# Revit family: RN 81084 Optipress-Segment de tuyau en acier inoxydable
name_source: partatom
category: Rohrformteile
units: mm (PartAtom-declared; Revit-internal decimal feet)

## family parameters
Arbeitsebenenbasiert = Nein
Beim Laden mit Abzugskörper schneiden = Nein
Bemaßung runder Anschluss = Durchmesser verwenden
Gemeinsam genutzt = Nein
Immer vertikal = Ja
Teiletyp = Nicht definiert

## types (11) — shared parameters
1.010.00.2 Number of the part of the guideline = 29
1.010.00.3 Issue date (month) of the guideline = 201308
1.010.00.4 Manufacturer name = R. Nussbaum AG
1.010.00.5 Revision date of the file = 20201220
1.100.00.4 Product designation = Optipress-Segment de tuyau en acier inoxydable
1.110.00.2 Index = 4
1.110.00.4 Product designation = Optipress
1.960/3L.00.8 Link (URL) = https://www.nussbaum.ch
29.700.00.4 Product name = Optipress-Segment de tuyau en acier inoxydable
29.700.00.5 Product identification = 2
29.700.00.6 Cross-sectional shape = 1
29.700.00.7 Nominal size system = DN
29.700.00.8 Nominal pressure system = PN
29.710.02.4 Nominal pressure = 16
29.710.02.5 max. allowed overpressure [hPa] = 1600
29.710.02.7 max. allowed continuous operating pressure [hPa] = 1600
29.710.02.9 max. allowed continuous operating temperature [°C] = 95
Connector Visibility = Nein
EnclosingSpace Visibility = Nein
Hersteller = R. Nussbaum AG
Typenkommentare = Optipress-Segment de tuyau en acier inoxydable
URL = https://www.nussbaum.ch

## per-type parameters (varying)
- DN=80: 1.800.00.3 BS number=01900400000000000000000000000000000000000000000055000000000000000009; 1.800.00.4 Comment field=81084.30, OP-Pezzo di tubo in acciaio inossidabile, DN=80, L=115; 1.810.00.3 Manufacturer’s reference number=81084.30; 1.810.00.4 DATANORM number=81084.30; 1.810.00.5 StLB number=261.152; 1.810.00.6 GTIN number=7612945692375; 29.710.02.10 Fitting weight [kg]=0.494; 29.710.02.3 Designation=OP-Pezzo di tubo in acciaio inossidabile, DN=80, L=115; CONNECTOR0_DIAMETER_dX_0r=80 mm; CONNECTOR0_dX_01=50 mm; CONNECTOR0_ref_dX=50 mm; CONNECTOR1_DIAMETER_dX_0r=80 mm; CONNECTOR1_dX_00=65 mm  [stored 0.213255 ft]; CONNECTOR1_dX_01=115 mm; CONNECTOR1_ref_dX=65 mm  [stored 0.213255 ft]; Modell=81084.30; R. Nussbaum AG 81084.22 it Visibility=Nein; R. Nussbaum AG 81084.23 it Visibility=Nein; R. Nussbaum AG 81084.24 it Visibility=Nein; R. Nussbaum AG 81084.25 it Visibility=Nein; R. Nussbaum AG 81084.26 it Visibility=Nein; R. Nussbaum AG 81084.27 it Visibility=Nein; R. Nussbaum AG 81084.28 it Visibility=Nein; R. Nussbaum AG 81084.29 it Visibility=Nein; R. Nussbaum AG 81084.30 it Visibility=Ja; R. Nussbaum AG 81084.31 it Visibility=Nein; R. Nussbaum AG 81084.32 it Visibility=Nein
- DN=60: 1.800.00.3 BS number=01900400000000000000000000000000000000000000000055000000000000000011; 1.800.00.4 Comment field=81084.32, OP-Pezzo di tubo in acciaio inossidabile, DN=60, L=101; 1.810.00.3 Manufacturer’s reference number=81084.32; 1.810.00.4 DATANORM number=81084.32; 1.810.00.5 StLB number=261.154; 1.810.00.6 GTIN number=7612945692351; 29.710.02.10 Fitting weight [kg]=0.307; 29.710.02.3 Designation=OP-Pezzo di tubo in acciaio inossidabile, DN=60, L=101; CONNECTOR0_DIAMETER_dX_0r=60 mm; CONNECTOR0_dX_01=43 mm  [stored 0.141076 ft]; CONNECTOR0_ref_dX=43 mm  [stored 0.141076 ft]; CONNECTOR1_DIAMETER_dX_0r=60 mm; CONNECTOR1_dX_00=58 mm; CONNECTOR1_dX_01=101 mm; CONNECTOR1_ref_dX=58 mm; Modell=81084.32; R. Nussbaum AG 81084.22 it Visibility=Nein; R. Nussbaum AG 81084.23 it Visibility=Nein; R. Nussbaum AG 81084.24 it Visibility=Nein; R. Nussbaum AG 81084.25 it Visibility=Nein; R. Nussbaum AG 81084.26 it Visibility=Nein; R. Nussbaum AG 81084.27 it Visibility=Nein; R. Nussbaum AG 81084.28 it Visibility=Nein; R. Nussbaum AG 81084.29 it Visibility=Nein; R. Nussbaum AG 81084.30 it Visibility=Nein; R. Nussbaum AG 81084.31 it Visibility=Nein; R. Nussbaum AG 81084.32 it Visibility=Ja
- DN=100: 1.800.00.3 BS number=01900400000000000000000000000000000000000000000055000000000000000010; 1.800.00.4 Comment field=81084.31, OP-Pezzo di tubo in acciaio inossidabile, DN=100, L=135; 1.810.00.3 Manufacturer’s reference number=81084.31; 1.810.00.4 DATANORM number=81084.31; 1.810.00.5 StLB number=261.153; 1.810.00.6 GTIN number=7612945692382; 29.710.02.10 Fitting weight [kg]=0.705; 29.710.02.3 Designation=OP-Pezzo di tubo in acciaio inossidabile, DN=100, L=135; CONNECTOR0_DIAMETER_dX_0r=100 mm  [stored 0.328084 ft]; CONNECTOR0_dX_01=60 mm; CONNECTOR0_ref_dX=60 mm; CONNECTOR1_DIAMETER_dX_0r=100 mm  [stored 0.328084 ft]; CONNECTOR1_dX_00=75 mm; CONNECTOR1_dX_01=135 mm; CONNECTOR1_ref_dX=75 mm; Modell=81084.31; R. Nussbaum AG 81084.22 it Visibility=Nein; R. Nussbaum AG 81084.23 it Visibility=Nein; R. Nussbaum AG 81084.24 it Visibility=Nein; R. Nussbaum AG 81084.25 it Visibility=Nein; R. Nussbaum AG 81084.26 it Visibility=Nein; R. Nussbaum AG 81084.27 it Visibility=Nein; R. Nussbaum AG 81084.28 it Visibility=Nein; R. Nussbaum AG 81084.29 it Visibility=Nein; R. Nussbaum AG 81084.30 it Visibility=Nein; R. Nussbaum AG 81084.31 it Visibility=Ja; R. Nussbaum AG 81084.32 it Visibility=Nein
- DN=65: 1.800.00.3 BS number=01900400000000000000000000000000000000000000000055000000000000000008; 1.800.00.4 Comment field=81084.29, OP-Pezzo di tubo in acciaio inossidabile, DN=65, L=115; 1.810.00.3 Manufacturer’s reference number=81084.29; 1.810.00.4 DATANORM number=81084.29; 1.810.00.5 StLB number=261.151; 1.810.00.6 GTIN number=7612945692368; 29.710.02.10 Fitting weight [kg]=0.426; 29.710.02.3 Designation=OP-Pezzo di tubo in acciaio inossidabile, DN=65, L=115; CONNECTOR0_DIAMETER_dX_0r=65 mm  [stored 0.213255 ft]; CONNECTOR0_dX_01=50 mm; CONNECTOR0_ref_dX=50 mm; CONNECTOR1_DIAMETER_dX_0r=65 mm  [stored 0.213255 ft]; CONNECTOR1_dX_00=65 mm  [stored 0.213255 ft]; CONNECTOR1_dX_01=115 mm; CONNECTOR1_ref_dX=65 mm  [stored 0.213255 ft]; Modell=81084.29; R. Nussbaum AG 81084.22 it Visibility=Nein; R. Nussbaum AG 81084.23 it Visibility=Nein; R. Nussbaum AG 81084.24 it Visibility=Nein; R. Nussbaum AG 81084.25 it Visibility=Nein; R. Nussbaum AG 81084.26 it Visibility=Nein; R. Nussbaum AG 81084.27 it Visibility=Nein; R. Nussbaum AG 81084.28 it Visibility=Nein; R. Nussbaum AG 81084.29 it Visibility=Ja; R. Nussbaum AG 81084.30 it Visibility=Nein; R. Nussbaum AG 81084.31 it Visibility=Nein; R. Nussbaum AG 81084.32 it Visibility=Nein
- DN=50: 1.800.00.3 BS number=01900400000000000000000000000000000000000000000055000000000000000007; 1.800.00.4 Comment field=81084.28, OP-Pezzo di tubo in acciaio inossidabile, DN=50, L=105; 1.810.00.3 Manufacturer’s reference number=81084.28; 1.810.00.4 DATANORM number=81084.28; 1.810.00.5 StLB number=261.148; 1.810.00.6 GTIN number=7612945692344; 29.710.02.10 Fitting weight [kg]=0.204; 29.710.02.3 Designation=OP-Pezzo di tubo in acciaio inossidabile, DN=50, L=105; CONNECTOR0_DIAMETER_dX_0r=50 mm; CONNECTOR0_dX_01=40 mm; CONNECTOR0_ref_dX=40 mm; CONNECTOR1_DIAMETER_dX_0r=50 mm; CONNECTOR1_dX_00=65 mm  [stored 0.213255 ft]; CONNECTOR1_dX_01=105 mm; CONNECTOR1_ref_dX=65 mm  [stored 0.213255 ft]; Modell=81084.28; R. Nussbaum AG 81084.22 it Visibility=Nein; R. Nussbaum AG 81084.23 it Visibility=Nein; R. Nussbaum AG 81084.24 it Visibility=Nein; R. Nussbaum AG 81084.25 it Visibility=Nein; R. Nussbaum AG 81084.26 it Visibility=Nein; R. Nussbaum AG 81084.27 it Visibility=Nein; R. Nussbaum AG 81084.28 it Visibility=Ja; R. Nussbaum AG 81084.29 it Visibility=Nein; R. Nussbaum AG 81084.30 it Visibility=Nein; R. Nussbaum AG 81084.31 it Visibility=Nein; R. Nussbaum AG 81084.32 it Visibility=Nein
- DN=40: 1.800.00.3 BS number=01900400000000000000000000000000000000000000000055000000000000000006; 1.800.00.4 Comment field=81084.27, OP-Pezzo di tubo in acciaio inossidabile, DN=40, L=87; 1.810.00.3 Manufacturer’s reference number=81084.27; 1.810.00.4 DATANORM number=81084.27; 1.810.00.5 StLB number=261.147; 1.810.00.6 GTIN number=7612945692337; 29.710.02.10 Fitting weight [kg]=0.124; 29.710.02.3 Designation=OP-Pezzo di tubo in acciaio inossidabile, DN=40, L=87; CONNECTOR0_DIAMETER_dX_0r=40 mm; CONNECTOR0_dX_01=36 mm  [stored 0.11811 ft]; CONNECTOR0_ref_dX=36 mm  [stored 0.11811 ft]; CONNECTOR1_DIAMETER_dX_0r=40 mm; CONNECTOR1_dX_00=51 mm; CONNECTOR1_dX_01=87 mm; CONNECTOR1_ref_dX=51 mm; Modell=81084.27; R. Nussbaum AG 81084.22 it Visibility=Nein; R. Nussbaum AG 81084.23 it Visibility=Nein; R. Nussbaum AG 81084.24 it Visibility=Nein; R. Nussbaum AG 81084.25 it Visibility=Nein; R. Nussbaum AG 81084.26 it Visibility=Nein; R. Nussbaum AG 81084.27 it Visibility=Ja; R. Nussbaum AG 81084.28 it Visibility=Nein; R. Nussbaum AG 81084.29 it Visibility=Nein; R. Nussbaum AG 81084.30 it Visibility=Nein; R. Nussbaum AG 81084.31 it Visibility=Nein; R. Nussbaum AG 81084.32 it Visibility=Nein
- DN=32: 1.800.00.3 BS number=01900400000000000000000000000000000000000000000055000000000000000005; 1.800.00.4 Comment field=81084.26, OP-Pezzo di tubo in acciaio inossidabile, DN=32, L=62; 1.810.00.3 Manufacturer’s reference number=81084.26; 1.810.00.4 DATANORM number=81084.26; 1.810.00.5 StLB number=261.146; 1.810.00.6 GTIN number=7612945692320; 29.710.02.10 Fitting weight [kg]=0.077; 29.710.02.3 Designation=OP-Pezzo di tubo in acciaio inossidabile, DN=32, L=62; CONNECTOR0_DIAMETER_dX_0r=32 mm; CONNECTOR0_dX_01=26 mm; CONNECTOR0_ref_dX=26 mm; CONNECTOR1_DIAMETER_dX_0r=32 mm; CONNECTOR1_dX_00=36 mm  [stored 0.11811 ft]; CONNECTOR1_dX_01=62 mm; CONNECTOR1_ref_dX=36 mm  [stored 0.11811 ft]; Modell=81084.26; R. Nussbaum AG 81084.22 it Visibility=Nein; R. Nussbaum AG 81084.23 it Visibility=Nein; R. Nussbaum AG 81084.24 it Visibility=Nein; R. Nussbaum AG 81084.25 it Visibility=Nein; R. Nussbaum AG 81084.26 it Visibility=Ja; R. Nussbaum AG 81084.27 it Visibility=Nein; R. Nussbaum AG 81084.28 it Visibility=Nein; R. Nussbaum AG 81084.29 it Visibility=Nein; R. Nussbaum AG 81084.30 it Visibility=Nein; R. Nussbaum AG 81084.31 it Visibility=Nein; R. Nussbaum AG 81084.32 it Visibility=Nein
- DN=25: 1.800.00.3 BS number=01900400000000000000000000000000000000000000000055000000000000000004; 1.800.00.4 Comment field=81084.25, OP-Pezzo di tubo in acciaio inossidabile, DN=25, L=58; 1.810.00.3 Manufacturer’s reference number=81084.25; 1.810.00.4 DATANORM number=81084.25; 1.810.00.5 StLB number=261.145; 1.810.00.6 GTIN number=7612945692313; 29.710.02.10 Fitting weight [kg]=0.046; 29.710.02.3 Designation=OP-Pezzo di tubo in acciaio inossidabile, DN=25, L=58; CONNECTOR0_DIAMETER_dX_0r=25 mm  [stored 0.082021 ft]; CONNECTOR0_dX_01=24 mm; CONNECTOR0_ref_dX=24 mm; CONNECTOR1_DIAMETER_dX_0r=25 mm  [stored 0.082021 ft]; CONNECTOR1_dX_00=34 mm; CONNECTOR1_dX_01=58 mm; CONNECTOR1_ref_dX=34 mm; Modell=81084.25; R. Nussbaum AG 81084.22 it Visibility=Nein; R. Nussbaum AG 81084.23 it Visibility=Nein; R. Nussbaum AG 81084.24 it Visibility=Nein; R. Nussbaum AG 81084.25 it Visibility=Ja; R. Nussbaum AG 81084.26 it Visibility=Nein; R. Nussbaum AG 81084.27 it Visibility=Nein; R. Nussbaum AG 81084.28 it Visibility=Nein; R. Nussbaum AG 81084.29 it Visibility=Nein; R. Nussbaum AG 81084.30 it Visibility=Nein; R. Nussbaum AG 81084.31 it Visibility=Nein; R. Nussbaum AG 81084.32 it Visibility=Nein
- DN=20: 1.800.00.3 BS number=01900400000000000000000000000000000000000000000055000000000000000003; 1.800.00.4 Comment field=81084.24, OP-Pezzo di tubo in acciaio inossidabile, DN=20, L=53; 1.810.00.3 Manufacturer’s reference number=81084.24; 1.810.00.4 DATANORM number=81084.24; 1.810.00.5 StLB number=261.144; 1.810.00.6 GTIN number=7612945692306; 29.710.02.10 Fitting weight [kg]=0.032; 29.710.02.3 Designation=OP-Pezzo di tubo in acciaio inossidabile, DN=20, L=53; CONNECTOR0_DIAMETER_dX_0r=20 mm; CONNECTOR0_dX_01=24 mm; CONNECTOR0_ref_dX=24 mm; CONNECTOR1_DIAMETER_dX_0r=20 mm; CONNECTOR1_dX_00=29 mm  [stored 0.0951444 ft]; CONNECTOR1_dX_01=53 mm; CONNECTOR1_ref_dX=29 mm  [stored 0.0951444 ft]; Modell=81084.24; R. Nussbaum AG 81084.22 it Visibility=Nein; R. Nussbaum AG 81084.23 it Visibility=Nein; R. Nussbaum AG 81084.24 it Visibility=Ja; R. Nussbaum AG 81084.25 it Visibility=Nein; R. Nussbaum AG 81084.26 it Visibility=Nein; R. Nussbaum AG 81084.27 it Visibility=Nein; R. Nussbaum AG 81084.28 it Visibility=Nein; R. Nussbaum AG 81084.29 it Visibility=Nein; R. Nussbaum AG 81084.30 it Visibility=Nein; R. Nussbaum AG 81084.31 it Visibility=Nein; R. Nussbaum AG 81084.32 it Visibility=Nein
- DN=15: 1.800.00.3 BS number=01900400000000000000000000000000000000000000000055000000000000000002; 1.800.00.4 Comment field=81084.23, OP-Pezzo di tubo in acciaio inossidabile, DN=15, L=49; 1.810.00.3 Manufacturer’s reference number=81084.23; 1.810.00.4 DATANORM number=81084.23; 1.810.00.5 StLB number=261.143; 1.810.00.6 GTIN number=7612945692290; 29.710.02.10 Fitting weight [kg]=0.02; 29.710.02.3 Designation=OP-Pezzo di tubo in acciaio inossidabile, DN=15, L=49; CONNECTOR0_DIAMETER_dX_0r=15 mm; CONNECTOR0_dX_01=22 mm; CONNECTOR0_ref_dX=22 mm; CONNECTOR1_DIAMETER_dX_0r=15 mm; CONNECTOR1_dX_00=27 mm; CONNECTOR1_dX_01=49 mm; CONNECTOR1_ref_dX=27 mm; Modell=81084.23; R. Nussbaum AG 81084.22 it Visibility=Nein; R. Nussbaum AG 81084.23 it Visibility=Ja; R. Nussbaum AG 81084.24 it Visibility=Nein; R. Nussbaum AG 81084.25 it Visibility=Nein; R. Nussbaum AG 81084.26 it Visibility=Nein; R. Nussbaum AG 81084.27 it Visibility=Nein; R. Nussbaum AG 81084.28 it Visibility=Nein; R. Nussbaum AG 81084.29 it Visibility=Nein; R. Nussbaum AG 81084.30 it Visibility=Nein; R. Nussbaum AG 81084.31 it Visibility=Nein; R. Nussbaum AG 81084.32 it Visibility=Nein
- DN=12: 1.800.00.3 BS number=01900400000000000000000000000000000000000000000055000000000000000001; 1.800.00.4 Comment field=81084.22, OP-Pezzo di tubo in acciaio inossidabile, DN=12, L=49; 1.810.00.3 Manufacturer’s reference number=81084.22; 1.810.00.4 DATANORM number=81084.22; 1.810.00.5 StLB number=261.142; 1.810.00.6 GTIN number=7612945692283; 29.710.02.10 Fitting weight [kg]=0.017; 29.710.02.3 Designation=OP-Pezzo di tubo in acciaio inossidabile, DN=12, L=49; CONNECTOR0_DIAMETER_dX_0r=12 mm  [stored 0.0393701 ft]; CONNECTOR0_dX_01=22 mm; CONNECTOR0_ref_dX=22 mm; CONNECTOR1_DIAMETER_dX_0r=12 mm  [stored 0.0393701 ft]; CONNECTOR1_dX_00=27 mm; CONNECTOR1_dX_01=49 mm; CONNECTOR1_ref_dX=27 mm; Modell=81084.22; R. Nussbaum AG 81084.22 it Visibility=Ja; R. Nussbaum AG 81084.23 it Visibility=Nein; R. Nussbaum AG 81084.24 it Visibility=Nein; R. Nussbaum AG 81084.25 it Visibility=Nein; R. Nussbaum AG 81084.26 it Visibility=Nein; R. Nussbaum AG 81084.27 it Visibility=Nein; R. Nussbaum AG 81084.28 it Visibility=Nein; R. Nussbaum AG 81084.29 it Visibility=Nein; R. Nussbaum AG 81084.30 it Visibility=Nein; R. Nussbaum AG 81084.31 it Visibility=Nein; R. Nussbaum AG 81084.32 it Visibility=Nein

note: [stored X ft] marks values corroborated as IEEE doubles in the binary element streams (Revit-internal decimal feet)

## geometry (parser evidence)
native form markers: Sweep x1
no freeform markers — native parametric forms only
